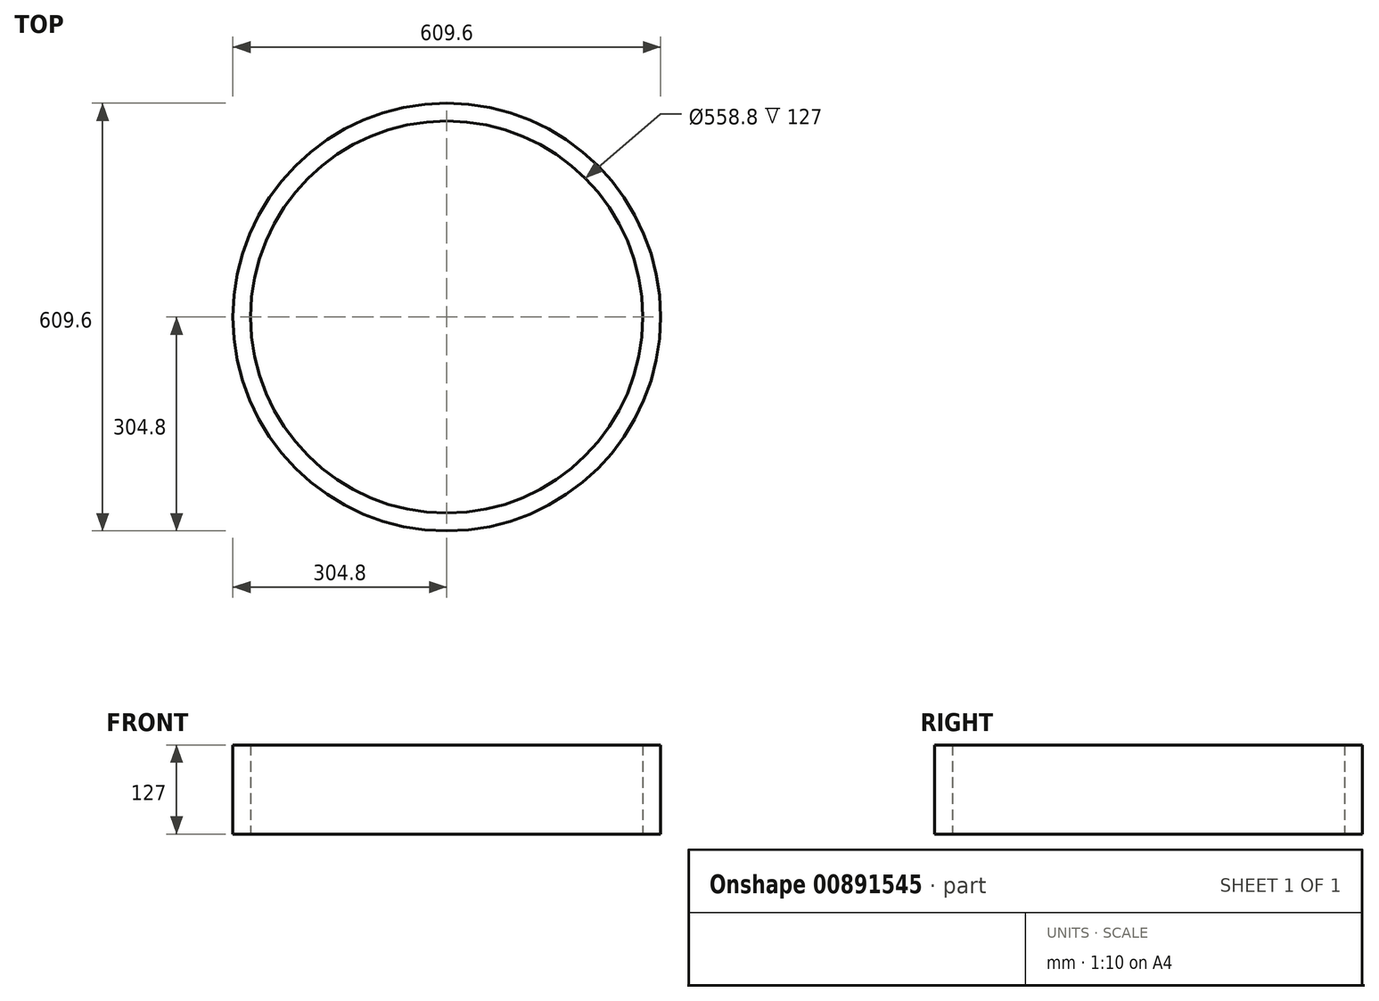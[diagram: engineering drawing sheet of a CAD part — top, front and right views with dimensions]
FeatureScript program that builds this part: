
annotation { "Feature Type Name" : "Feature", "Feature Type Description" : "" }
export const myFeature = defineFeature(function(context is Context, id is Id, definition is map)
    precondition{}
    {
        {
            var Q0;
            Q0=qCreatedBy(makeId("Top.planeOp"),FACE);
            var sketch = newSketch(context, id + "F0", { "sketchPlane" : qUnion([Q0])});
            skCircle(sketch, "E0", {"center": v(0, 0) * mm, "radius": 279.4 * mm});
            skCircle(sketch, "E1", {"center": v(0, 0) * mm, "radius": 304.8 * mm});
            skSolve(sketch);
        }
        {
            var Q0;
            Q0 = qSketchRegion(id + "F0", true);
            extrude(context, id + "F1", {"entities" : qUnion([Q0]), "depth" : 127 * mm, "offsetDistance" : 25.4 * mm});
        }
    });
